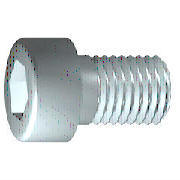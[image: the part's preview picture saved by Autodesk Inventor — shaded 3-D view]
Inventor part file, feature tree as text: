
AUTODESK INVENTOR PART (.ipt)
format: ipt  version: 2019 (Build 230136000, 136)  size: 196,608 bytes
history: native  units: mm (DEFAULTED — no unit token found)
features: sketch x2, extrude x1, plane x1, fillet x1
ambient origin geometry x7: Origin, YZ Plane, XY Plane, X Axis, Y Axis, Z Axis, Center Point
bodies: Solid1 (feature_tree), Body (feature_tree)
feature tree (5):
  extrude  "Slot"  Depth=5.0mm
  plane  "Work Plane1"
  fillet  "Fillet2"  Radius=5.0mm
  sketch  "Sketch1"  dims[d1=14.0mm d2=0.49086mm d3=5.0mm]
  sketch  "Sketch2"  dims[d4=2.5mm d5=60.0deg d6=5.0mm d7=5.0mm d8=4.618802mm d9=8.5mm d10=90.0deg d11=10.0mm d12=0.0mm d13=14.0mm d14=0.0mm d15=0.49076mm d16=0.49076mm d17=0.5mm d19=0.0mm d26=16.0mm d27=45.0deg d28=0.0mm d29=0.0mm d30=0.1mm]
